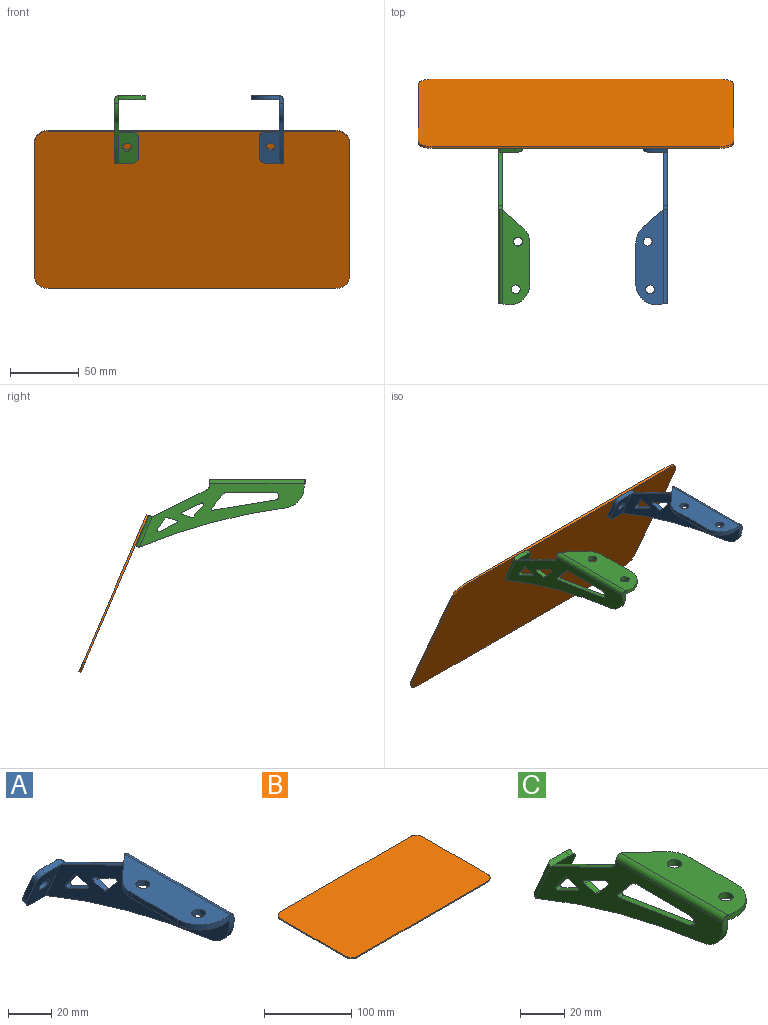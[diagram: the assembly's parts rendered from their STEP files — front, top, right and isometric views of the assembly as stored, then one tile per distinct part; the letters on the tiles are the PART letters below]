
ASSEMBLY  parts=3 mates=6
PART A: 44 faces, bbox 22.8x123.8x49.4 mm
  f0: plane 120.3x46.4mm, normal (-1,0,0), area 1889.9mm2, adj f5,f6,f7,f8,f9,f10,f19,f20
  f1: plane 120.3x46.4mm, normal (1,0,0), area 1889.9mm2, adj f6,f7,f8,f9,f15,f16,f19,f20
  f2: plane 30.13x3mm, normal (-1,0,0), area 90.4mm2, adj f4,f5,f21,f22
  f3: plane 14.79x13.21mm, normal (-0.67,0.75,0), area 59.5mm2, adj f4,f5,f7,f22
  f4: plane 69.53x19.79mm, normal (0,0,1), area 1079.3mm2, adj f2,f3,f16,f21,f22,f23,f24
  f5: plane 69.53x19.79mm, normal (0,0,-1), area 1079.3mm2, adj f0,f2,f3,f21,f22,f23,f24
  f6: plane 5.69x3mm, normal (0,-1,0), area 15.1mm2, adj f0,f1,f16,f20,f21
  f7: plane 3.27x3mm, normal (0,1,0), area 7.9mm2, adj f0,f1,f3,f16,f19
  f8: plane 39.21x19.44mm, normal (0,0.44,0.9), area 131.3mm2, adj f0,f1,f12,f19
  f9: extruded ~107.27x28.84mm, area 334.2mm2, adj f0,f1,f11,f20
  f10: plane 22.21x14.5mm, normal (0,-0.92,-0.4), area 306.8mm2, adj f0,f11,f12,f13,f17,f18,f25
  f11: plane 12.5x2.76mm, normal (0,0.4,-0.92), area 35.6mm2, adj f9,f10,f14,f15,f18
  f12: plane 12.5x2.76mm, normal (0,-0.4,0.92), area 35.6mm2, adj f8,f10,f14,f15,f17
  f13: plane 14.21x8.37mm, normal (-1,0,0), area 42.6mm2, adj f10,f14,f17,f18
  f14: plane 22.21x14.5mm, normal (0,0.92,0.4), area 306.8mm2, adj f11,f12,f13,f15,f17,f18,f25
  f15: cylinder r=3mm len=23.4mm, axis (0,0.4,-0.92), area 114mm2, adj f1,f11,f12,f14
  f16: cylinder r=3mm len=68.74mm, axis (0,-1,0), area 323.9mm2, adj f1,f4,f6,f7
  f17: cylinder r=5mm len=5.78mm, axis (0,-0.92,-0.4), area 23.6mm2, adj f10,f12,f13,f14
  f18: cylinder r=5mm len=5.78mm, axis (0,0.92,0.4), area 23.6mm2, adj f10,f11,f13,f14
  f19: cylinder r=5mm len=4.48mm, axis (1,0,0), area 16.7mm2, adj f0,f1,f7,f8
  f20: cylinder r=15mm len=14.87mm, axis (-1,0,0), area 64.8mm2, adj f0,f1,f6,f9
  f21: cylinder r=15mm len=19.79mm, axis (0,0,-1), area 85.3mm2, adj f2,f4,f5,f6
  f22: cylinder r=15mm len=11.19mm, axis (0,0,-1), area 37.9mm2, adj f2,f3,f4,f5
  f23: cylinder r=3.25mm len=6.5mm, axis (0,0,1), area 61.3mm2, adj f4,f5
  f24: cylinder r=3.25mm len=6.5mm, axis (0,0,1), area 61.3mm2, adj f4,f5
  f25: cylinder r=3.25mm len=7.16mm, axis (0,0.92,0.4), area 61.3mm2, adj f10,f14
  f26: plane 8.64x7.23mm, normal (0,0.77,0.64), area 33.8mm2, adj f0,f1,f39,f41
  f27: plane 14.12x6.57mm, normal (0,-0.42,-0.91), area 46.7mm2, adj f0,f1,f39,f40
  f28: plane 6.89x3mm, normal (0,-0.29,0.96), area 21.6mm2, adj f0,f1,f40,f41
  f29: plane 7.06x3mm, normal (0,0.29,-0.96), area 22.1mm2, adj f0,f1,f36,f38
  f30: plane 8.47x5.79mm, normal (0,-0.83,-0.56), area 30.8mm2, adj f0,f1,f37,f38
  f31: plane 12.84x6.35mm, normal (0,0.44,0.9), area 43mm2, adj f0,f1,f36,f37
  f32: plane 35.26x3mm, normal (0,0,-1), area 105.8mm2, adj f0,f1,f35,f43
  f33: plane 10.34x8.66mm, normal (0,-0.77,-0.64), area 40.4mm2, adj f0,f1,f42,f43
  f34: plane 45.73x7.53mm, normal (0,0.16,0.99), area 139mm2, adj f0,f1,f35,f42
  f35: cylinder r=2.77mm len=5.51mm, axis (1,0,0), area 24.8mm2, adj f0,f1,f32,f34
  f36: cylinder r=1mm len=3mm, axis (-1,0,0), area 7.2mm2, adj f0,f1,f29,f31
  f37: cylinder r=1mm len=3mm, axis (-1,0,0), area 7.9mm2, adj f0,f1,f30,f31
  f38: cylinder r=1mm len=3mm, axis (-1,0,0), area 3.8mm2, adj f0,f1,f29,f30
  f39: cylinder r=1mm len=3mm, axis (-1,0,0), area 8.1mm2, adj f0,f1,f26,f27
  f40: cylinder r=1mm len=3mm, axis (-1,0,0), area 7.2mm2, adj f0,f1,f27,f28
  f41: cylinder r=1mm len=3mm, axis (-1,0,0), area 3.5mm2, adj f0,f1,f26,f28
  f42: cylinder r=1mm len=3mm, axis (-1,0,0), area 7.3mm2, adj f0,f1,f33,f34
  f43: cylinder r=3mm len=3mm, axis (1,0,0), area 7.9mm2, adj f0,f1,f32,f33
PART B: 10 faces, bbox 230x125x1.5 mm
  f0: plane 210x1.5mm, normal (0,1,0), area 315mm2, adj f4,f5,f6,f9
  f1: plane 105x1.5mm, normal (-1,0,0), area 157.5mm2, adj f4,f5,f6,f7
  f2: plane 210x1.5mm, normal (0,-1,0), area 315mm2, adj f4,f5,f7,f8
  f3: plane 105x1.5mm, normal (1,0,0), area 157.5mm2, adj f4,f5,f8,f9
  f4: plane 230x125mm, normal (0,0,1), area 28664.2mm2, adj f0,f1,f2,f3,f6,f7,f8,f9
  f5: plane 230x125mm, normal (0,0,-1), area 28664.2mm2, adj f0,f1,f2,f3,f6,f7,f8,f9
  f6: cylinder r=10mm len=10mm, axis (0,0,1), area 23.6mm2, adj f0,f1,f4,f5
  f7: cylinder r=10mm len=10mm, axis (0,0,-1), area 23.6mm2, adj f1,f2,f4,f5
  f8: cylinder r=10mm len=10mm, axis (0,0,1), area 23.6mm2, adj f2,f3,f4,f5
  f9: cylinder r=10mm len=10mm, axis (0,0,-1), area 23.6mm2, adj f0,f3,f4,f5
PART C: 44 faces, bbox 22.8x123.8x49.4 mm
  f0: plane 120.3x46.4mm, normal (1,0,0), area 1889.9mm2, adj f5,f6,f7,f8,f9,f10,f19,f20
  f1: plane 120.3x46.4mm, normal (-1,0,0), area 1889.9mm2, adj f6,f7,f8,f9,f15,f16,f19,f20
  f2: plane 30.13x3mm, normal (1,0,0), area 90.4mm2, adj f4,f5,f21,f22
  f3: plane 14.79x13.21mm, normal (0.67,0.75,0), area 59.5mm2, adj f4,f5,f7,f22
  f4: plane 69.53x19.79mm, normal (0,0,1), area 1079.3mm2, adj f2,f3,f16,f21,f22,f23,f24
  f5: plane 69.53x19.79mm, normal (0,0,-1), area 1079.3mm2, adj f0,f2,f3,f21,f22,f23,f24
  f6: plane 5.69x3mm, normal (0,-1,0), area 15.1mm2, adj f0,f1,f16,f20,f21
  f7: plane 3.27x3mm, normal (0,1,0), area 7.9mm2, adj f0,f1,f3,f16,f19
  f8: plane 39.21x19.44mm, normal (0,0.44,0.9), area 131.3mm2, adj f0,f1,f12,f19
  f9: extruded ~107.27x28.84mm, area 334.2mm2, adj f0,f1,f11,f20
  f10: plane 22.21x14.5mm, normal (0,-0.92,-0.4), area 306.8mm2, adj f0,f11,f12,f13,f17,f18,f25
  f11: plane 12.5x2.76mm, normal (0,0.4,-0.92), area 35.6mm2, adj f9,f10,f14,f15,f18
  f12: plane 12.5x2.76mm, normal (0,-0.4,0.92), area 35.6mm2, adj f8,f10,f14,f15,f17
  f13: plane 14.21x8.37mm, normal (1,0,0), area 42.6mm2, adj f10,f14,f17,f18
  f14: plane 22.21x14.5mm, normal (0,0.92,0.4), area 306.8mm2, adj f11,f12,f13,f15,f17,f18,f25
  f15: cylinder r=3mm len=23.4mm, axis (0,0.4,-0.92), area 114mm2, adj f1,f11,f12,f14
  f16: cylinder r=3mm len=68.74mm, axis (0,-1,0), area 323.9mm2, adj f1,f4,f6,f7
  f17: cylinder r=5mm len=5.78mm, axis (0,-0.92,-0.4), area 23.6mm2, adj f10,f12,f13,f14
  f18: cylinder r=5mm len=5.78mm, axis (0,0.92,0.4), area 23.6mm2, adj f10,f11,f13,f14
  f19: cylinder r=5mm len=4.48mm, axis (-1,0,0), area 16.7mm2, adj f0,f1,f7,f8
  f20: cylinder r=15mm len=14.87mm, axis (1,0,0), area 64.8mm2, adj f0,f1,f6,f9
  f21: cylinder r=15mm len=19.79mm, axis (0,0,-1), area 85.3mm2, adj f2,f4,f5,f6
  f22: cylinder r=15mm len=11.19mm, axis (0,0,-1), area 37.9mm2, adj f2,f3,f4,f5
  f23: cylinder r=3.25mm len=6.5mm, axis (0,0,1), area 61.3mm2, adj f4,f5
  f24: cylinder r=3.25mm len=6.5mm, axis (0,0,1), area 61.3mm2, adj f4,f5
  f25: cylinder r=3.25mm len=7.16mm, axis (0,0.92,0.4), area 61.3mm2, adj f10,f14
  f26: plane 8.64x7.23mm, normal (0,0.77,0.64), area 33.8mm2, adj f0,f1,f39,f41
  f27: plane 14.12x6.57mm, normal (0,-0.42,-0.91), area 46.7mm2, adj f0,f1,f39,f40
  f28: plane 6.89x3mm, normal (0,-0.29,0.96), area 21.6mm2, adj f0,f1,f40,f41
  f29: plane 7.06x3mm, normal (0,0.29,-0.96), area 22.1mm2, adj f0,f1,f36,f38
  f30: plane 8.47x5.79mm, normal (0,-0.83,-0.56), area 30.8mm2, adj f0,f1,f37,f38
  f31: plane 12.84x6.35mm, normal (0,0.44,0.9), area 43mm2, adj f0,f1,f36,f37
  f32: plane 35.26x3mm, normal (0,0,-1), area 105.8mm2, adj f0,f1,f35,f43
  f33: plane 10.34x8.66mm, normal (0,-0.77,-0.64), area 40.4mm2, adj f0,f1,f42,f43
  f34: plane 45.73x7.53mm, normal (0,0.16,0.99), area 139mm2, adj f0,f1,f35,f42
  f35: cylinder r=2.77mm len=5.51mm, axis (-1,0,0), area 24.8mm2, adj f0,f1,f32,f34
  f36: cylinder r=1mm len=3mm, axis (1,0,0), area 7.2mm2, adj f0,f1,f29,f31
  f37: cylinder r=1mm len=3mm, axis (1,0,0), area 7.9mm2, adj f0,f1,f30,f31
  f38: cylinder r=1mm len=3mm, axis (1,0,0), area 3.8mm2, adj f0,f1,f29,f30
  f39: cylinder r=1mm len=3mm, axis (1,0,0), area 8.1mm2, adj f0,f1,f26,f27
  f40: cylinder r=1mm len=3mm, axis (1,0,0), area 7.2mm2, adj f0,f1,f27,f28
  f41: cylinder r=1mm len=3mm, axis (1,0,0), area 3.5mm2, adj f0,f1,f26,f28
  f42: cylinder r=1mm len=3mm, axis (1,0,0), area 7.3mm2, adj f0,f1,f33,f34
  f43: cylinder r=3mm len=3mm, axis (-1,0,0), area 7.9mm2, adj f0,f1,f32,f33
PLACE A t=(-3.65,-52.56,107.95)mm
PLACE B rot(axis=(-1,0,0),66.7deg) t=(36.12,45.64,14.94)mm
PLACE C t=(-8.39,-52.56,107.95)mm
MATE planar C.f4 <-> A.f4  axis (0,0,1) through (-5.51,-67.02,110.95)mm
MATE planar C.f12 <-> B.f2  axis (0,-0.4,0.92) through (-10.96,14.03,84.33)mm
MATE planar A.f18 <-> B.f5  axis (0,0.92,0.4) through (92.98,23.05,67.33)mm
MATE parallel A.f21 <-> C.f4  axis (0,0,1) through (97.69,-83.82,110.95)mm
MATE parallel B.f4 <-> A.f17  axis (0,0.92,0.4) through (38.97,41.58,28.15)mm
MATE planar B.f5 <-> C.f14  axis (0,-0.92,-0.4) through (38.97,40.2,27.55)mm
